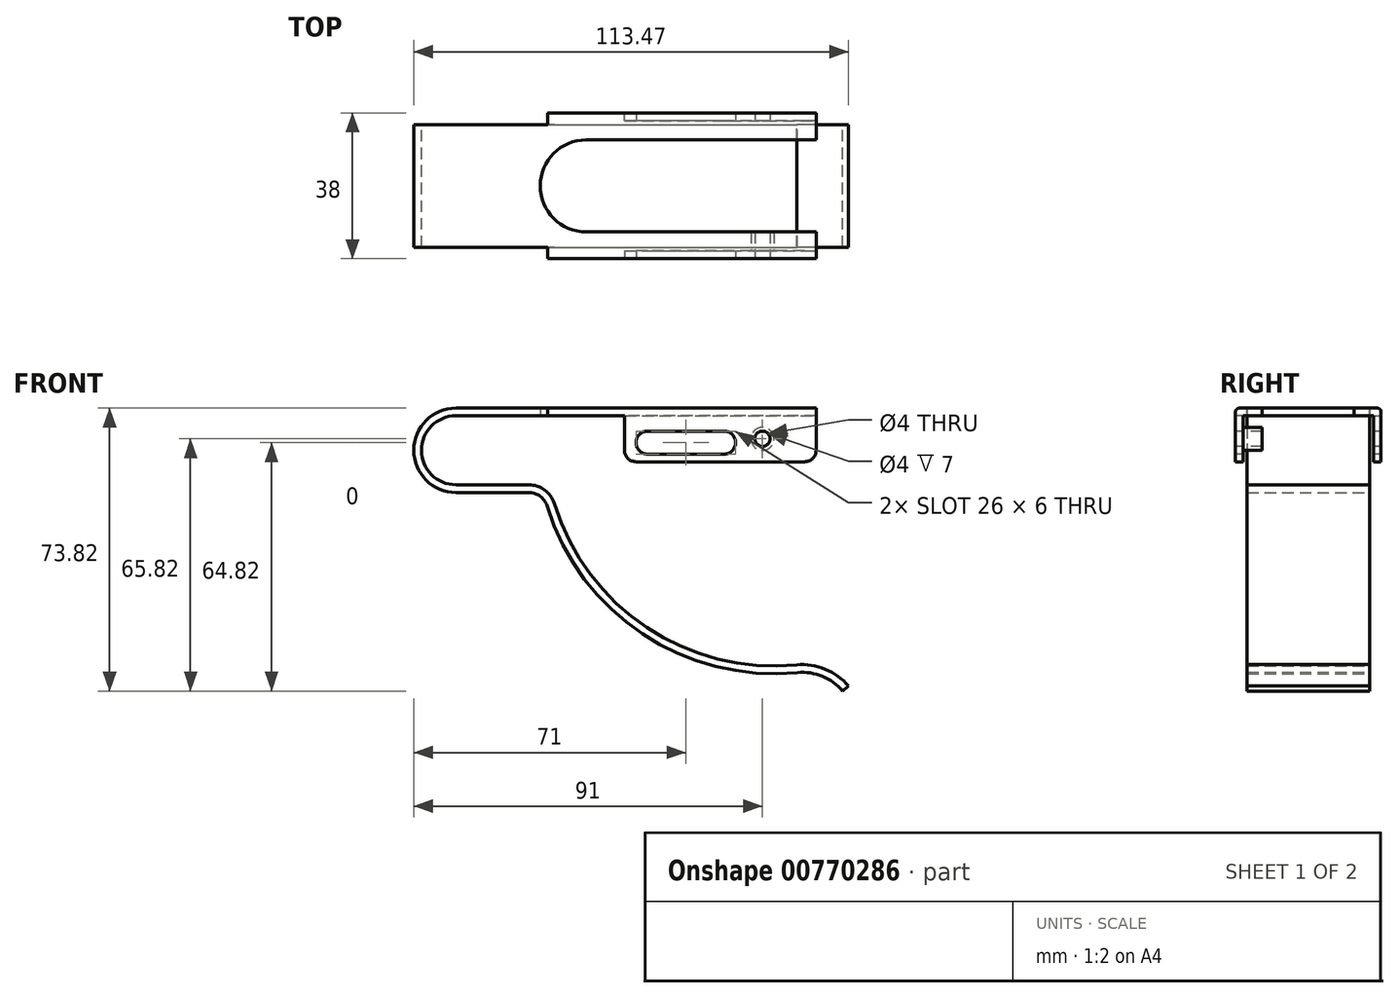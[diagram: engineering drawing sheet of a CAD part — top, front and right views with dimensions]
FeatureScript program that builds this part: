
annotation { "Feature Type Name" : "Feature", "Feature Type Description" : "" }
export const myFeature = defineFeature(function(context is Context, id is Id, definition is map)
    precondition{}
    {
        {
            var Q0;
            Q0=qCreatedBy(makeId("Front.planeOp"),FACE);
            var sketch = newSketch(context, id + "F0", { "sketchPlane" : qUnion([Q0])});
            skArc(sketch, "E0", {"start": v(0, 11) * mm, "mid": v(-11, 0) * mm, "end": v(0, -11) * mm});
            skLineSegment(sketch, "E1", {"start": v(0, 11) * mm, "end": v(94, 11) * mm});
            skLineSegment(sketch, "E2", {"start": v(0, -11) * mm, "end": v(19, -11) * mm});
            skArc(sketch, "E3", {"start": v(23.78, -14.53) * mm, "mid": v(48.7, -47.92) * mm, "end": v(89.14, -58) * mm});
            skArc(sketch, "E4", {"start": v(100.95, -62.82) * mm, "mid": v(95.63, -58.98) * mm, "end": v(89.14, -58) * mm});
            skPoint(sketch, "E5.visualSharp", {"position": v(22.8, -11) * mm});
            skArc(sketch, "E5.filletArc", {"start": v(23.78, -14.53) * mm, "mid": v(21.97, -11.98) * mm, "end": v(19, -11) * mm});
            skLineSegment(sketch, "E6.0", {"start": v(0, 9) * mm, "end": v(94, 9) * mm});
            skArc(sketch, "E6.1", {"start": v(0, 9) * mm, "mid": v(-9, 0) * mm, "end": v(0, -9) * mm});
            skArc(sketch, "E6.2", {"start": v(102.47, -61.52) * mm, "mid": v(96.38, -57.13) * mm, "end": v(88.95, -56) * mm});
            skArc(sketch, "E6.3", {"start": v(25.7, -13.94) * mm, "mid": v(49.82, -46.26) * mm, "end": v(88.95, -56) * mm});
            skArc(sketch, "E6.4", {"start": v(25.7, -13.94) * mm, "mid": v(23.16, -10.37) * mm, "end": v(19, -9) * mm});
            skLineSegment(sketch, "E6.5", {"start": v(0, -9) * mm, "end": v(19, -9) * mm});
            skLineSegment(sketch, "E7", {"start": v(100.95, -62.82) * mm, "end": v(102.47, -61.52) * mm});
            skLineSegment(sketch, "E8", {"start": v(94, 9) * mm, "end": v(94, 11) * mm});
            skSolve(sketch);
        }
        {
            var Q0;
            Q0 = qSketchRegion(id + "F0", true);
            extrude(context, id + "F1", {"entities" : qUnion([Q0]), "depth" : 16 * mm, "offsetDistance" : 25 * mm});
        }
        {
            var Q0;
            Q0=makeQuery(id+"F1.opExtrude","SWEPT_FACE",FACE,{"disambiguationData":[OSD([sQuery(id+"F0.wireOp",EDGE,"E1")])]});
            var sketch = newSketch(context, id + "F2", { "sketchPlane" : qUnion([Q0])});
            skLineSegment(sketch, "E9.bottom", {"start": v(94, -16) * mm, "end": v(24, -16) * mm});
            skLineSegment(sketch, "E9.top", {"start": v(94, -19) * mm, "end": v(24, -19) * mm});
            skLineSegment(sketch, "E9.left", {"start": v(94, -16) * mm, "end": v(94, -19) * mm});
            skLineSegment(sketch, "E9.right", {"start": v(24, -16) * mm, "end": v(24, -19) * mm});
            skSolve(sketch);
        }
        {
            var Q0;
            Q0 = qSketchRegion(id + "F2", true);
            extrude(context, id + "F3", {"entities" : qUnion([Q0]), "operationType" : NewBodyOperationType.ADD, "oppositeDirection" : true, "depth" : 2 * mm, "offsetDistance" : 25 * mm});
        }
        {
            var Q0;
            Q0=makeQuery(id+"F3.opExtrude","SWEPT_FACE",FACE,{"disambiguationData":[OSD([sQuery(id+"F2.wireOp",EDGE,"E9.top")])]});
            var sketch = newSketch(context, id + "F4", { "sketchPlane" : qUnion([Q0])});
            skLineSegment(sketch, "E10.bottom", {"start": v(94, 11) * mm, "end": v(44, 11) * mm});
            skLineSegment(sketch, "E10.top", {"start": v(94, -3) * mm, "end": v(44, -3) * mm});
            skLineSegment(sketch, "E10.left", {"start": v(94, 11) * mm, "end": v(94, -3) * mm});
            skLineSegment(sketch, "E10.right", {"start": v(44, 11) * mm, "end": v(44, -3) * mm});
            skSolve(sketch);
        }
        {
            var Q0;
            Q0 = qSketchRegion(id + "F4", true);
            extrude(context, id + "F5", {"entities" : qUnion([Q0]), "operationType" : NewBodyOperationType.ADD, "oppositeDirection" : true, "depth" : 2 * mm, "offsetDistance" : 25 * mm});
        }
        {
            var Q0;
            Q0=makeQuery(id+"F3.opExtrude","CAP_EDGE",EDGE,{"disambiguationData":[OSD([sQuery(id+"F2.wireOp",EDGE,"E9.top")])],"isStart":true});
            fillet(context, id + "F6", {"entities" : qUnion([Q0]), "radius" : 1 * mm, "allowEdgeOverflow" : false});
        }
        {
            var Q0;
            Q0=makeQuery(id+"F1.opExtrude","SWEPT_BODY",BODY,{"disambiguationData":[OSD([sQuery(id+"F0.wireOp",EDGE,"E0"),sQuery(id+"F0.wireOp",EDGE,"E1"),sQuery(id+"F0.wireOp",EDGE,"E2"),sQuery(id+"F0.wireOp",EDGE,"E3"),sQuery(id+"F0.wireOp",EDGE,"E4"),sQuery(id+"F0.wireOp",EDGE,"E5.filletArc"),sQuery(id+"F0.wireOp",EDGE,"E6.0"),sQuery(id+"F0.wireOp",EDGE,"E6.1"),sQuery(id+"F0.wireOp",EDGE,"E6.2"),sQuery(id+"F0.wireOp",EDGE,"E6.3"),sQuery(id+"F0.wireOp",EDGE,"E6.4"),sQuery(id+"F0.wireOp",EDGE,"E6.5"),sQuery(id+"F0.wireOp",EDGE,"E7"),sQuery(id+"F0.wireOp",EDGE,"E8")])]});
            var Q1;
            Q1=qCreatedBy(makeId("Front.planeOp"),FACE);
            mirror(context, id + "F7", {"operationType" : NewBodyOperationType.ADD, "entities" : qUnion([Q0]), "mirrorPlane" : qUnion([Q1])});
        }
        {
            var Q0;
            Q0=qCreatedBy(makeId("Top.planeOp"),FACE);
            var sketch = newSketch(context, id + "F8", { "sketchPlane" : qUnion([Q0])});
            skArc(sketch, "E11", {"start": v(34, 12) * mm, "mid": v(22, 0) * mm, "end": v(34, -12) * mm});
            skLineSegment(sketch, "E12", {"start": v(34, 12) * mm, "end": v(94, 12) * mm});
            skLineSegment(sketch, "E13", {"start": v(34, -12) * mm, "end": v(94, -12) * mm});
            skLineSegment(sketch, "E14", {"start": v(94, -12) * mm, "end": v(94, 12) * mm});
            skSolve(sketch);
        }
        {
            var Q0;
            Q0 = qSketchRegion(id + "F8", true);
            extrude(context, id + "F9", {"entities" : qUnion([Q0]), "operationType" : NewBodyOperationType.REMOVE, "depth" : 32.3 * mm, "offsetDistance" : 25 * mm});
        }
        {
            var Q0;
            Q0=makeQuery(id+"F5.boolean.opBoolean","MERGE",FACE,{"derivedFrom":[makeQuery(id+"F3.opExtrude","SWEPT_FACE",FACE,{"disambiguationData":[OSD([sQuery(id+"F2.wireOp",EDGE,"E9.top")])]}),makeQuery(id+"F5.opExtrude","CAP_FACE",FACE,{"disambiguationData":[OSD([sQuery(id+"F4.wireOp",EDGE,"E10.bottom"),sQuery(id+"F4.wireOp",EDGE,"E10.top"),sQuery(id+"F4.wireOp",EDGE,"E10.left"),sQuery(id+"F4.wireOp",EDGE,"E10.right")])],"isStart":true})]});
            var sketch = newSketch(context, id + "F10", { "sketchPlane" : qUnion([Q0])});
            skLineSegment(sketch, "E15", {"start": v(50, 2) * mm, "end": v(70, 2) * mm});
            skArc(sketch, "E16.0.startCap", {"start": v(50, -1) * mm, "mid": v(47, 2) * mm, "end": v(50, 5) * mm});
            skArc(sketch, "E16.0.endCap", {"start": v(70, 5) * mm, "mid": v(73, 2) * mm, "end": v(70, -1) * mm});
            skLineSegment(sketch, "E16.0.left", {"start": v(50, 5) * mm, "end": v(70, 5) * mm});
            skLineSegment(sketch, "E16.0.right", {"start": v(50, -1) * mm, "end": v(70, -1) * mm});
            skSolve(sketch);
        }
        {
            var Q0;
            Q0 = qSketchRegion(id + "F10", true);
            extrude(context, id + "F11", {"entities" : qUnion([Q0]), "operationType" : NewBodyOperationType.REMOVE, "endBound" : BoundingType.THROUGH_ALL, "oppositeDirection" : true, "depth" : 25 * mm, "offsetDistance" : 25 * mm});
        }
        {
            var Q0;
            Q0=makeQuery(id+"F5.boolean.opBoolean","MERGE",FACE,{"derivedFrom":[makeQuery(id+"F3.opExtrude","SWEPT_FACE",FACE,{"disambiguationData":[OSD([sQuery(id+"F2.wireOp",EDGE,"E9.top")])]}),makeQuery(id+"F5.opExtrude","CAP_FACE",FACE,{"disambiguationData":[OSD([sQuery(id+"F4.wireOp",EDGE,"E10.bottom"),sQuery(id+"F4.wireOp",EDGE,"E10.top"),sQuery(id+"F4.wireOp",EDGE,"E10.left"),sQuery(id+"F4.wireOp",EDGE,"E10.right")])],"isStart":true})]});
            var sketch = newSketch(context, id + "F12", { "sketchPlane" : qUnion([Q0])});
            skPoint(sketch, "E17", {"position": v(80, 3) * mm});
            skSolve(sketch);
        }
        {
            var Q0;
            Q0=sQuery(id+"F12.wireOp",VERTEX,"E17");
            var Q1;
            Q1=makeQuery(id+"F1.opExtrude","SWEPT_BODY",BODY,{"disambiguationData":[OSD([sQuery(id+"F0.wireOp",EDGE,"E0"),sQuery(id+"F0.wireOp",EDGE,"E1"),sQuery(id+"F0.wireOp",EDGE,"E2"),sQuery(id+"F0.wireOp",EDGE,"E3"),sQuery(id+"F0.wireOp",EDGE,"E4"),sQuery(id+"F0.wireOp",EDGE,"E5.filletArc"),sQuery(id+"F0.wireOp",EDGE,"E6.0"),sQuery(id+"F0.wireOp",EDGE,"E6.1"),sQuery(id+"F0.wireOp",EDGE,"E6.2"),sQuery(id+"F0.wireOp",EDGE,"E6.3"),sQuery(id+"F0.wireOp",EDGE,"E6.4"),sQuery(id+"F0.wireOp",EDGE,"E6.5"),sQuery(id+"F0.wireOp",EDGE,"E7"),sQuery(id+"F0.wireOp",EDGE,"E8")])]});
            hole(context, id + "F13", {"style" : HoleStyle.SIMPLE, "endStyle" : HoleEndStyle.THROUGH, "holeDiameter" : 4 * mm, "majorDiameter" : 5 * mm, "isTappedThrough" : true, "tappedDepth" : 12 * mm, "tapClearance" : 3, "locations" : qUnion([Q0]), "scope" : qUnion([Q1])});
        }
        {
            var Q0;
            Q0=makeQuery(id+"F5.opExtrude","CAP_FACE",FACE,{"disambiguationData":[OSD([sQuery(id+"F4.wireOp",EDGE,"E10.bottom"),sQuery(id+"F4.wireOp",EDGE,"E10.top"),sQuery(id+"F4.wireOp",EDGE,"E10.left"),sQuery(id+"F4.wireOp",EDGE,"E10.right")])],"isStart":false});
            var sketch = newSketch(context, id + "F14", { "sketchPlane" : qUnion([Q0])});
            skCircle(sketch, "E18.0", {"center": v(-80, 3) * mm, "radius": 2 * mm});
            skCircle(sketch, "E19.0", {"center": v(-80, 3) * mm, "radius": 3 * mm});
            skSolve(sketch);
        }
        {
            var Q0;
            Q0 = qSketchRegion(id + "F14", true);
            extrude(context, id + "F15", {"entities" : qUnion([Q0]), "operationType" : NewBodyOperationType.ADD, "depth" : 5 * mm, "offsetDistance" : 25 * mm});
        }
        {
            var Q0;
            Q0=makeQuery(id+"F5.opExtrude","SWEPT_EDGE",EDGE,{"disambiguationData":[OSD([sQuery(id+"F4.wireOp",EDGE,"E10.top"),sQuery(id+"F4.wireOp",EDGE,"E10.left")])]});
            var Q1;
            Q1=makeQuery(id+"F7.opPattern","COPY",EDGE,{"derivedFrom":makeQuery(id+"F5.opExtrude","SWEPT_EDGE",EDGE,{"disambiguationData":[OSD([sQuery(id+"F4.wireOp",EDGE,"E10.top"),sQuery(id+"F4.wireOp",EDGE,"E10.left")])]}),"instanceName":"1"});
            var Q2;
            Q2=makeQuery(id+"F5.opExtrude","SWEPT_EDGE",EDGE,{"disambiguationData":[OSD([sQuery(id+"F4.wireOp",EDGE,"E10.top"),sQuery(id+"F4.wireOp",EDGE,"E10.right")])]});
            var Q3;
            Q3=makeQuery(id+"F7.opPattern","COPY",EDGE,{"derivedFrom":makeQuery(id+"F5.opExtrude","SWEPT_EDGE",EDGE,{"disambiguationData":[OSD([sQuery(id+"F4.wireOp",EDGE,"E10.top"),sQuery(id+"F4.wireOp",EDGE,"E10.right")])]}),"instanceName":"1"});
            fillet(context, id + "F16", {"entities" : qUnion([Q0, Q1, Q2, Q3]), "radius" : 3 * mm, "tangentPropagation" : true, "allowEdgeOverflow" : false});
        }
    });
